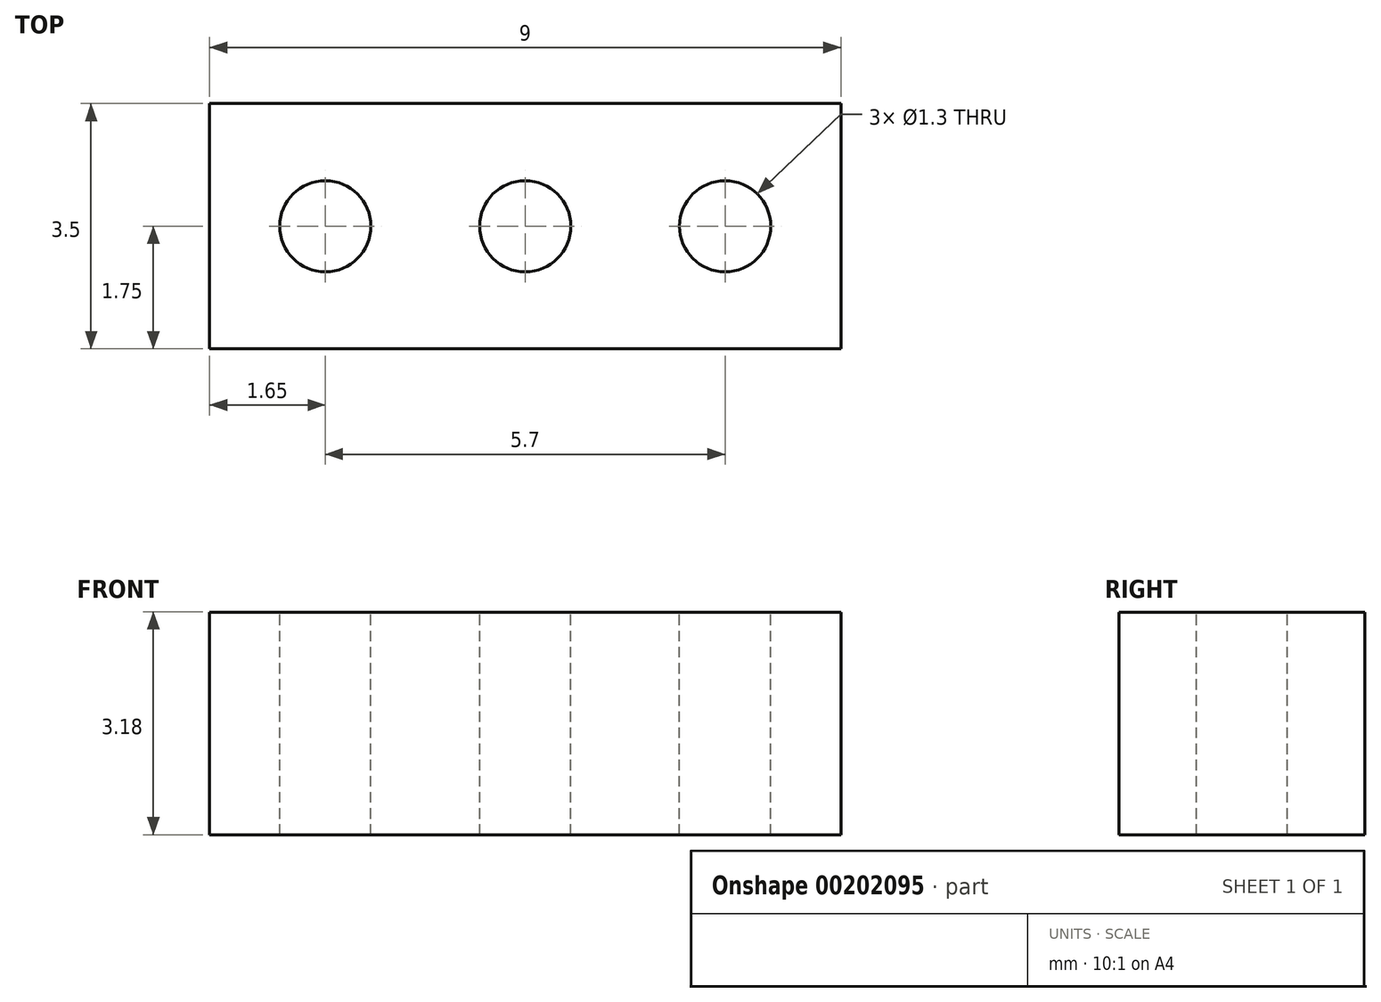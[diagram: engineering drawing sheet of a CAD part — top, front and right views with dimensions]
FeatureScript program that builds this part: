
annotation { "Feature Type Name" : "Feature", "Feature Type Description" : "" }
export const myFeature = defineFeature(function(context is Context, id is Id, definition is map)
    precondition{}
    {
        {
            var Q0;
            Q0=qCreatedBy(makeId("Top.planeOp"),FACE);
            var sketch = newSketch(context, id + "F0", { "sketchPlane" : qUnion([Q0])});
            skLineSegment(sketch, "E0.bottom", {"start": v(-4.5, 1.75) * mm, "end": v(4.5, 1.75) * mm});
            skLineSegment(sketch, "E0.top", {"start": v(-4.5, -1.75) * mm, "end": v(4.5, -1.75) * mm});
            skLineSegment(sketch, "E0.left", {"start": v(-4.5, 1.75) * mm, "end": v(-4.5, -1.75) * mm});
            skLineSegment(sketch, "E0.right", {"start": v(4.5, 1.75) * mm, "end": v(4.5, -1.75) * mm});
            skPoint(sketch, "E0.middle", {"position": v(0, 0) * mm});
            skSolve(sketch);
        }
        {
            var Q0;
            Q0 = qSketchRegion(id + "F0", true);
            extrude(context, id + "F1", {"entities" : qUnion([Q0]), "depth" : 3.17 * mm});
        }
        {
            var Q0;
            Q0=makeQuery(id+"F1.opExtrude","CAP_FACE",FACE,{"disambiguationData":[OSD([sQuery(id+"F0.wireOp",EDGE,"E0.bottom"),sQuery(id+"F0.wireOp",EDGE,"E0.top"),sQuery(id+"F0.wireOp",EDGE,"E0.left"),sQuery(id+"F0.wireOp",EDGE,"E0.right")])],"isStart":false});
            var sketch = newSketch(context, id + "F2", { "sketchPlane" : qUnion([Q0])});
            skPoint(sketch, "E1", {"position": v(0, 0) * mm});
            skPoint(sketch, "E2", {"position": v(-2.85, 0) * mm});
            skPoint(sketch, "E3", {"position": v(2.85, 0) * mm});
            skSolve(sketch);
        }
        {
            var Q0;
            Q0=sQuery(id+"F2.wireOp",VERTEX,"E1");
            var Q1;
            Q1=sQuery(id+"F2.wireOp",VERTEX,"E2");
            var Q2;
            Q2=sQuery(id+"F2.wireOp",VERTEX,"E3");
            var Q3;
            Q3=makeQuery(id+"F1.opExtrude","SWEPT_BODY",BODY,{"disambiguationData":[OSD([sQuery(id+"F0.wireOp",EDGE,"E0.bottom"),sQuery(id+"F0.wireOp",EDGE,"E0.top"),sQuery(id+"F0.wireOp",EDGE,"E0.left"),sQuery(id+"F0.wireOp",EDGE,"E0.right")])]});
            hole(context, id + "F3", {"style" : HoleStyle.SIMPLE, "endStyle" : HoleEndStyle.THROUGH, "holeDiameter" : 1.3 * mm, "locations" : qUnion([Q0, Q1, Q2]), "scope" : qUnion([Q3]), "isTappedThrough" : true});
        }
    });
